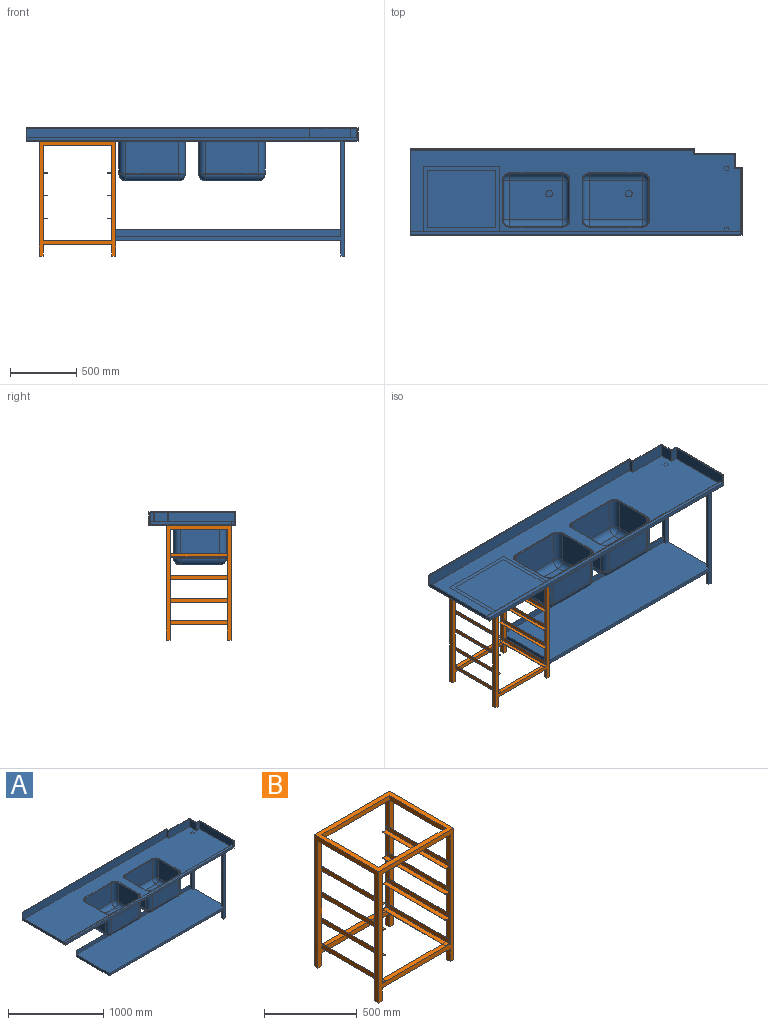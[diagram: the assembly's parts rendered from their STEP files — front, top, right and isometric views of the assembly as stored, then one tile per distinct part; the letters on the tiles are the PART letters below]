
ASSEMBLY  parts=2 mates=1
PART A: 143 faces, bbox 2500x650x965 mm
  f0: plane 715x30mm, normal (0,-1,0), area 21450mm2, adj f15,f94,f96,f121
  f1: plane 120x30mm, normal (-1,0,0), area 3600mm2, adj f93,f95,f97,f122
  f2: plane 715x30mm, normal (-1,0,0), area 21450mm2, adj f3,f15,f98,f121
  f3: plane 715x30mm, normal (0,1,0), area 21450mm2, adj f2,f15,f94,f121
  f4: plane 2488x28mm, normal (0,1,0), area 69664mm2, adj f5,f18,f32,f118
  f5: plane 2488x610mm, normal (0,0,1), area 1090860.9mm2, adj f4,f16,f17,f18,f19,f20,f21,f102
  f6: plane 650x100mm, normal (-1,0,0), area 20200mm2, adj f7,f8,f14,f15,f17,f32
  f7: plane 2500x100mm, normal (0,-1,0), area 75700mm2, adj f6,f8,f9,f15,f18,f32
  f8: plane 2500x650mm, normal (0,0,1), area 31400mm2, adj f6,f7,f9,f10,f11,f12,f13,f14
  f9: plane 510x100mm, normal (1,0,0), area 51000mm2, adj f7,f8,f10,f15
  f10: plane 100x50mm, normal (0,1,0), area 5000mm2, adj f8,f9,f11,f15
  f11: plane 105x100mm, normal (1,0,0), area 10500mm2, adj f8,f10,f12,f15
  f12: plane 305x100mm, normal (0,1,0), area 30500mm2, adj f8,f11,f13,f15
  f13: plane 100x35mm, normal (1,0,0), area 3500mm2, adj f8,f12,f14,f15
  f14: plane 2145x100mm, normal (0,1,0), area 214500mm2, adj f6,f8,f13,f15
  f15: plane 2500x650mm, normal (0,0,-1), area 1209817mm2, adj f0,f2,f3,f6,f7,f9,f10,f11
  f16: plane 98x35mm, normal (-1,0,0), area 3430mm2, adj f5,f8,f17,f21
  f17: plane 2135x98mm, normal (0,-1,0), area 209174mm2, adj f5,f6,f8,f16,f32,f118
  f18: plane 500x98mm, normal (-1,0,0), area 48160mm2, adj f4,f5,f7,f8,f19,f32
  f19: plane 98x50mm, normal (0,-1,0), area 4900mm2, adj f5,f8,f18,f20
  f20: plane 105x98mm, normal (-1,0,0), area 10290mm2, adj f5,f8,f19,f21
  f21: plane 305x98mm, normal (0,-1,0), area 29890mm2, adj f5,f8,f16,f20
  f22: plane 300x248mm, normal (-1,0,0), area 74400mm2, adj f15,f81,f87,f90
  f23: plane 400x248mm, normal (0,-1,0), area 99200mm2, adj f15,f79,f81,f82
  f24: plane 300x248mm, normal (1,0,0), area 74400mm2, adj f15,f79,f83,f84
  f25: plane 400x248mm, normal (0,1,0), area 99200mm2, adj f15,f84,f88,f90
  f26: plane 400x300mm, normal (0,0,-1), area 118036.5mm2, adj f82,f83,f87,f88,f92
  f27: plane 300x248mm, normal (-1,0,0), area 74400mm2, adj f15,f72,f76,f78
  f28: plane 400x248mm, normal (0,-1,0), area 99200mm2, adj f15,f69,f75,f78
  f29: plane 300x248mm, normal (1,0,0), area 74400mm2, adj f15,f67,f69,f70
  f30: plane 400x248mm, normal (0,1,0), area 99200mm2, adj f15,f67,f71,f72
  f31: plane 400x300mm, normal (0,0,-1), area 118036.5mm2, adj f70,f71,f75,f76,f91
  f32: plane 2490x640mm, normal (0,0,1), area 75920mm2, adj f4,f6,f7,f17,f18,f118
  f33: plane 396x296mm, normal (0,0,1), area 115252.5mm2, adj f46,f47,f51,f52,f92
  f34: plane 396x242mm, normal (0,-1,0), area 95832mm2, adj f45,f51,f54,f110
  f35: plane 296x242mm, normal (-1,0,0), area 71632mm2, adj f43,f45,f46,f114
  f36: plane 396x242mm, normal (0,1,0), area 95832mm2, adj f43,f47,f48,f117
  f37: plane 296x242mm, normal (1,0,0), area 71632mm2, adj f48,f52,f54,f113
  f38: plane 396x296mm, normal (0,0,1), area 115252.5mm2, adj f58,f59,f63,f64,f91
  f39: plane 396x242mm, normal (0,-1,0), area 95832mm2, adj f55,f57,f58,f102
  f40: plane 296x242mm, normal (-1,0,0), area 71632mm2, adj f55,f59,f60,f106
  f41: plane 396x242mm, normal (0,1,0), area 95832mm2, adj f60,f64,f66,f109
  f42: plane 296x242mm, normal (1,0,0), area 71632mm2, adj f57,f63,f66,f105
  f43: cylinder r=50mm len=242mm, axis (0,0,1), area 19006.6mm2, adj f35,f36,f44,f116
  f44: sphere r=50mm, area 3927mm2, adj f43,f46,f47
  f45: cylinder r=50mm len=242mm, axis (0,0,-1), area 19006.6mm2, adj f34,f35,f49,f112
  f46: cylinder r=50mm len=296mm, axis (0,1,0), area 23247.8mm2, adj f33,f35,f44,f49
  f47: cylinder r=50mm len=396mm, axis (1,0,0), area 31101.8mm2, adj f33,f36,f44,f50
  f48: cylinder r=50mm len=242mm, axis (0,0,-1), area 19006.6mm2, adj f36,f37,f50,f115
  f49: sphere r=50mm, area 3927mm2, adj f45,f46,f51
  f50: sphere r=50mm, area 3927mm2, adj f47,f48,f52
  f51: cylinder r=50mm len=396mm, axis (-1,0,0), area 31101.8mm2, adj f33,f34,f49,f53
  f52: cylinder r=50mm len=296mm, axis (0,-1,0), area 23247.8mm2, adj f33,f37,f50,f53
  f53: sphere r=50mm, area 3927mm2, adj f51,f52,f54
  f54: cylinder r=50mm len=242mm, axis (0,0,1), area 19006.6mm2, adj f34,f37,f53,f111
  f55: cylinder r=50mm len=242mm, axis (0,0,-1), area 19006.6mm2, adj f39,f40,f56,f104
  f56: sphere r=50mm, area 3927mm2, adj f55,f58,f59
  f57: cylinder r=50mm len=242mm, axis (0,0,1), area 19006.6mm2, adj f39,f42,f61,f103
  f58: cylinder r=50mm len=396mm, axis (-1,0,0), area 31101.8mm2, adj f38,f39,f56,f61
  f59: cylinder r=50mm len=296mm, axis (0,1,0), area 23247.8mm2, adj f38,f40,f56,f62
  f60: cylinder r=50mm len=242mm, axis (0,0,1), area 19006.6mm2, adj f40,f41,f62,f108
  f61: sphere r=50mm, area 3927mm2, adj f57,f58,f63
  f62: sphere r=50mm, area 3927mm2, adj f59,f60,f64
  f63: cylinder r=50mm len=296mm, axis (0,-1,0), area 23247.8mm2, adj f38,f42,f61,f65
  f64: cylinder r=50mm len=396mm, axis (1,0,0), area 31101.8mm2, adj f38,f41,f62,f65
  f65: sphere r=50mm, area 3927mm2, adj f63,f64,f66
  f66: cylinder r=50mm len=242mm, axis (0,0,-1), area 19006.6mm2, adj f41,f42,f65,f107
  f67: cylinder r=50mm len=248mm, axis (0,0,1), area 19477.9mm2, adj f15,f29,f30,f68
  f68: sphere r=50mm, area 3927mm2, adj f67,f70,f71
  f69: cylinder r=50mm len=248mm, axis (0,0,-1), area 19477.9mm2, adj f15,f28,f29,f73
  f70: cylinder r=50mm len=300mm, axis (0,-1,0), area 23561.9mm2, adj f29,f31,f68,f73
  f71: cylinder r=50mm len=400mm, axis (1,0,0), area 31415.9mm2, adj f30,f31,f68,f74
  f72: cylinder r=50mm len=248mm, axis (0,0,-1), area 19477.9mm2, adj f15,f27,f30,f74
  f73: sphere r=50mm, area 3927mm2, adj f69,f70,f75
  f74: sphere r=50mm, area 3927mm2, adj f71,f72,f76
  f75: cylinder r=50mm len=400mm, axis (-1,0,0), area 31415.9mm2, adj f28,f31,f73,f77
  f76: cylinder r=50mm len=300mm, axis (0,1,0), area 23561.9mm2, adj f27,f31,f74,f77
  f77: sphere r=50mm, area 3927mm2, adj f75,f76,f78
  f78: cylinder r=50mm len=248mm, axis (0,0,1), area 19477.9mm2, adj f15,f27,f28,f77
  f79: cylinder r=50mm len=248mm, axis (0,0,-1), area 19477.9mm2, adj f15,f23,f24,f80
  f80: sphere r=50mm, area 3927mm2, adj f79,f82,f83
  f81: cylinder r=50mm len=248mm, axis (0,0,1), area 19477.9mm2, adj f15,f22,f23,f85
  f82: cylinder r=50mm len=400mm, axis (-1,0,0), area 31415.9mm2, adj f23,f26,f80,f85
  f83: cylinder r=50mm len=300mm, axis (0,-1,0), area 23561.9mm2, adj f24,f26,f80,f86
  f84: cylinder r=50mm len=248mm, axis (0,0,1), area 19477.9mm2, adj f15,f24,f25,f86
  f85: sphere r=50mm, area 3927mm2, adj f81,f82,f87
  f86: sphere r=50mm, area 3927mm2, adj f83,f84,f88
  f87: cylinder r=50mm len=300mm, axis (0,1,0), area 23561.9mm2, adj f22,f26,f85,f89
  f88: cylinder r=50mm len=400mm, axis (1,0,0), area 31415.9mm2, adj f25,f26,f86,f89
  f89: sphere r=50mm, area 3927mm2, adj f87,f88,f90
  f90: cylinder r=50mm len=248mm, axis (0,0,-1), area 19477.9mm2, adj f15,f22,f25,f89
  f91: cylinder r=25mm len=50mm, axis (0,0,1), area 314.2mm2, adj f31,f38
  f92: cylinder r=25mm len=50mm, axis (0,0,1), area 314.2mm2, adj f26,f33
  f93: plane 1725x865mm, normal (0,1,0), area 161550mm2, adj f1,f15,f94,f96,f97,f119,f122,f123
  f94: plane 865x490mm, normal (1,0,0), area 64800mm2, adj f0,f3,f15,f93,f95,f97,f98,f100
  f95: plane 120x30mm, normal (0,-1,0), area 3600mm2, adj f1,f94,f97,f122
  f96: plane 715x30mm, normal (-1,0,0), area 21350mm2, adj f0,f15,f93,f119,f120,f121
  f97: plane 30x30mm, normal (0,0,-1), area 900mm2, adj f1,f93,f94,f95
  f98: plane 1725x865mm, normal (0,-1,0), area 76800mm2, adj f2,f15,f94,f99,f101,f121,f122,f123
  f99: plane 120x30mm, normal (-1,0,0), area 3600mm2, adj f98,f100,f101,f122
  f100: plane 120x30mm, normal (0,1,0), area 3600mm2, adj f94,f99,f101,f122
  f101: plane 30x30mm, normal (0,0,-1), area 900mm2, adj f94,f98,f99,f100
  f102: cylinder r=6mm len=396mm, axis (1,0,0), area 3732.2mm2, adj f5,f39,f103,f104
  f103: torus R=56mm, axis (0,0,1), area 772.5mm2, adj f5,f57,f102,f105
  f104: torus R=56mm, axis (0,0,1), area 772.5mm2, adj f5,f55,f102,f106
  f105: cylinder r=6mm len=296mm, axis (0,1,0), area 2789.7mm2, adj f5,f42,f103,f107
  f106: cylinder r=6mm len=296mm, axis (0,-1,0), area 2789.7mm2, adj f5,f40,f104,f108
  f107: torus R=56mm, axis (0,0,1), area 772.5mm2, adj f5,f66,f105,f109
  f108: torus R=56mm, axis (0,0,1), area 772.5mm2, adj f5,f60,f106,f109
  f109: cylinder r=6mm len=396mm, axis (-1,0,0), area 3732.2mm2, adj f5,f41,f107,f108
  f110: cylinder r=6mm len=396mm, axis (1,0,0), area 3732.2mm2, adj f5,f34,f111,f112
  f111: torus R=56mm, axis (0,0,1), area 772.5mm2, adj f5,f54,f110,f113
  f112: torus R=56mm, axis (0,0,1), area 772.5mm2, adj f5,f45,f110,f114
  f113: cylinder r=6mm len=296mm, axis (0,1,0), area 2789.7mm2, adj f5,f37,f111,f115
  f114: cylinder r=6mm len=296mm, axis (0,-1,0), area 2789.7mm2, adj f5,f35,f112,f116
  f115: torus R=56mm, axis (0,0,1), area 772.5mm2, adj f5,f48,f113,f117
  f116: torus R=56mm, axis (0,0,1), area 772.5mm2, adj f5,f43,f114,f117
  f117: cylinder r=6mm len=396mm, axis (-1,0,0), area 3732.2mm2, adj f5,f36,f115,f116
  f118: plane 610x28mm, normal (1,0,0), area 17080mm2, adj f4,f5,f17,f32
  f119: plane 1695x2mm, normal (0,0,1), area 3390mm2, adj f93,f96,f120,f123
  f120: plane 1695x50mm, normal (0,-1,0), area 84750mm2, adj f96,f119,f121,f123
  f121: plane 1725x488mm, normal (0,0,1), area 840060mm2, adj f0,f2,f3,f94,f96,f98,f120,f123
  f122: plane 1725x490mm, normal (0,0,-1), area 843450mm2, adj f1,f93,f94,f95,f98,f99,f100,f123
  f123: plane 490x80mm, normal (-1,0,0), area 14800mm2, adj f93,f98,f119,f120,f121,f122
  f124: plane 2496x646mm, normal (0,0,1), area 83556mm2, adj f125,f126,f127,f129,f130,f131,f132,f133
  f125: plane 96x6mm, normal (1,0,0), area 576mm2, adj f124,f128,f134,f136
  f126: plane 26x26mm, normal (1,0,0), area 676mm2, adj f124,f127,f137,f142
  f127: plane 2496x96mm, normal (0,1,0), area 65316mm2, adj f124,f126,f128,f129,f138,f142
  f128: plane 2496x646mm, normal (0,0,-1), area 18816mm2, adj f125,f127,f129,f130,f131,f132,f133,f134
  f129: plane 506x96mm, normal (-1,0,0), area 48576mm2, adj f124,f127,f128,f130
  f130: plane 96x50mm, normal (0,-1,0), area 4800mm2, adj f124,f128,f129,f131
  f131: plane 105x96mm, normal (-1,0,0), area 10080mm2, adj f124,f128,f130,f132
  f132: plane 305x96mm, normal (0,-1,0), area 29280mm2, adj f124,f128,f131,f133
  f133: plane 96x35mm, normal (-1,0,0), area 3360mm2, adj f124,f128,f132,f134
  f134: plane 2141x96mm, normal (0,-1,0), area 205536mm2, adj f124,f125,f128,f133
  f135: plane 96x35mm, normal (1,0,0), area 3360mm2, adj f124,f128,f136,f141
  f136: plane 2135x96mm, normal (0,1,0), area 204960mm2, adj f124,f125,f128,f135
  f137: plane 2490x26mm, normal (0,-1,0), area 64740mm2, adj f124,f126,f138,f142
  f138: plane 500x96mm, normal (1,0,0), area 47324mm2, adj f124,f127,f128,f137,f139,f142
  f139: plane 96x50mm, normal (0,1,0), area 4800mm2, adj f124,f128,f138,f140
  f140: plane 105x96mm, normal (1,0,0), area 10080mm2, adj f124,f128,f139,f141
  f141: plane 305x96mm, normal (0,1,0), area 29280mm2, adj f124,f128,f135,f140
  f142: plane 2490x26mm, normal (0,0,-1), area 64740mm2, adj f126,f127,f137,f138
PART B: 127 faces, bbox 575x490x865 mm
  f0: plane 720x30mm, normal (-1,0,0), area 18621.5mm2, adj f3,f18,f20,f26,f82,f84,f90,f93
  f1: plane 515x30mm, normal (0,0,1), area 13960.7mm2, adj f5,f6,f8,f12,f35,f38,f39,f83
  f2: plane 720x30mm, normal (1,0,0), area 18621.5mm2, adj f3,f18,f20,f26,f34,f36,f42,f45
  f3: plane 515x30mm, normal (0,0,1), area 13960.7mm2, adj f0,f2,f18,f20,f36,f38,f40,f84
  f4: plane 515x30mm, normal (0,1,0), area 15450mm2, adj f10,f17,f28,f29
  f5: plane 835x575mm, normal (0,1,0), area 65550mm2, adj f1,f6,f7,f9,f11,f12,f13,f14
  f6: plane 720x30mm, normal (1,0,0), area 18621.5mm2, adj f1,f5,f8,f17,f34,f35,f41,f45
  f7: plane 865x490mm, normal (-1,0,0), area 64800mm2, adj f5,f8,f10,f11,f18,f20,f22,f27
  f8: plane 865x575mm, normal (0,-1,0), area 82800mm2, adj f1,f6,f7,f9,f10,f11,f12,f13
  f9: plane 85x30mm, normal (1,0,0), area 2550mm2, adj f5,f8,f11,f16
  f10: plane 575x490mm, normal (0,0,1), area 60300mm2, adj f4,f7,f8,f13,f20,f21,f28,f29
  f11: plane 30x30mm, normal (0,0,-1), area 900mm2, adj f5,f7,f8,f9
  f12: plane 720x30mm, normal (-1,0,0), area 18621.5mm2, adj f1,f5,f8,f17,f82,f83,f89,f93
  f13: plane 865x490mm, normal (1,0,0), area 64800mm2, adj f5,f8,f10,f15,f18,f20,f24,f30
  f14: plane 85x30mm, normal (-1,0,0), area 2550mm2, adj f5,f8,f15,f16
  f15: plane 30x30mm, normal (0,0,-1), area 900mm2, adj f5,f8,f13,f14
  f16: plane 515x30mm, normal (0,0,-1), area 15450mm2, adj f5,f8,f9,f14
  f17: plane 515x30mm, normal (0,0,-1), area 15450mm2, adj f4,f6,f8,f12
  f18: plane 835x575mm, normal (0,-1,0), area 65550mm2, adj f0,f2,f3,f7,f13,f19,f22,f23
  f19: plane 85x30mm, normal (1,0,0), area 2550mm2, adj f18,f20,f22,f25
  f20: plane 865x575mm, normal (0,1,0), area 82800mm2, adj f0,f2,f3,f7,f10,f13,f19,f22
  f21: plane 515x30mm, normal (0,-1,0), area 15450mm2, adj f10,f26,f28,f29
  f22: plane 30x30mm, normal (0,0,-1), area 900mm2, adj f7,f18,f19,f20
  f23: plane 85x30mm, normal (-1,0,0), area 2550mm2, adj f18,f20,f24,f25
  f24: plane 30x30mm, normal (0,0,-1), area 900mm2, adj f13,f18,f20,f23
  f25: plane 515x30mm, normal (0,0,-1), area 15450mm2, adj f18,f19,f20,f23
  f26: plane 515x30mm, normal (0,0,-1), area 15450mm2, adj f0,f2,f20,f21
  f27: plane 430x30mm, normal (0,0,-1), area 12900mm2, adj f5,f7,f18,f28
  f28: plane 430x30mm, normal (1,0,0), area 12900mm2, adj f4,f10,f21,f27
  f29: plane 430x30mm, normal (-1,0,0), area 12900mm2, adj f4,f10,f21,f30
  f30: plane 430x30mm, normal (0,0,-1), area 12900mm2, adj f5,f13,f18,f29
  f31: plane 430x30mm, normal (0,0,-1), area 12900mm2, adj f5,f18,f32,f38
  f32: plane 430x30mm, normal (-1,0,0), area 12900mm2, adj f5,f18,f31,f34
  f33: plane 480x28.5mm, normal (1,0,0), area 13669.3mm2, adj f34,f35,f36,f37,f41,f42
  f34: plane 470x1.5mm, normal (0,0,1), area 705mm2, adj f2,f6,f32,f33,f41,f42
  f35: plane 25x25mm, normal (0,-1,0), area 72.8mm2, adj f1,f6,f33,f37,f39,f41
  f36: plane 25x25mm, normal (0,1,0), area 72.8mm2, adj f2,f3,f33,f37,f40,f42
  f37: plane 480x28.5mm, normal (0,0,1), area 13669.3mm2, adj f33,f35,f36,f38,f39,f40
  f38: plane 470x1.5mm, normal (1,0,0), area 705mm2, adj f1,f3,f31,f37,f39,f40
  f39: cylinder r=5mm len=5mm, axis (0,0,1), area 11.8mm2, adj f1,f35,f37,f38
  f40: cylinder r=5mm len=5mm, axis (0,0,-1), area 11.8mm2, adj f3,f36,f37,f38
  f41: cylinder r=5mm len=5mm, axis (-1,0,0), area 11.8mm2, adj f6,f33,f34,f35
  f42: cylinder r=5mm len=5mm, axis (1,0,0), area 11.8mm2, adj f2,f33,f34,f36
  f43: plane 430x30mm, normal (-1,0,0), area 12900mm2, adj f5,f18,f45,f47
  f44: plane 480x28.5mm, normal (1,0,0), area 13669.3mm2, adj f45,f46,f48,f49,f53,f54
  f45: plane 470x1.5mm, normal (0,0,1), area 705mm2, adj f2,f6,f43,f44,f53,f54
  f46: plane 25x25mm, normal (0,-1,0), area 72.8mm2, adj f6,f44,f47,f49,f52,f54
  f47: plane 480x30mm, normal (0,0,-1), area 14389.3mm2, adj f2,f6,f43,f46,f48,f50,f51,f52
  f48: plane 25x25mm, normal (0,1,0), area 72.8mm2, adj f2,f44,f47,f49,f51,f53
  f49: plane 480x28.5mm, normal (0,0,1), area 13669.3mm2, adj f44,f46,f48,f50,f51,f52
  f50: plane 470x1.5mm, normal (1,0,0), area 705mm2, adj f47,f49,f51,f52
  f51: cylinder r=5mm len=5mm, axis (0,0,-1), area 11.8mm2, adj f47,f48,f49,f50
  f52: cylinder r=5mm len=5mm, axis (0,0,1), area 11.8mm2, adj f46,f47,f49,f50
  f53: cylinder r=5mm len=5mm, axis (1,0,0), area 11.8mm2, adj f2,f44,f45,f48
  f54: cylinder r=5mm len=5mm, axis (-1,0,0), area 11.8mm2, adj f6,f44,f45,f46
  f55: plane 430x30mm, normal (-1,0,0), area 12900mm2, adj f5,f18,f57,f59
  f56: plane 480x28.5mm, normal (1,0,0), area 13669.3mm2, adj f57,f58,f60,f61,f65,f66
  f57: plane 470x1.5mm, normal (0,0,1), area 705mm2, adj f2,f6,f55,f56,f65,f66
  f58: plane 25x25mm, normal (0,-1,0), area 72.8mm2, adj f6,f56,f59,f61,f64,f65
  f59: plane 480x30mm, normal (0,0,-1), area 14389.3mm2, adj f2,f6,f55,f58,f60,f62,f63,f64
  f60: plane 25x25mm, normal (0,1,0), area 72.8mm2, adj f2,f56,f59,f61,f63,f66
  f61: plane 480x28.5mm, normal (0,0,1), area 13669.3mm2, adj f56,f58,f60,f62,f63,f64
  f62: plane 470x1.5mm, normal (1,0,0), area 705mm2, adj f59,f61,f63,f64
  f63: cylinder r=5mm len=5mm, axis (0,0,-1), area 11.8mm2, adj f59,f60,f61,f62
  f64: cylinder r=5mm len=5mm, axis (0,0,1), area 11.8mm2, adj f58,f59,f61,f62
  f65: cylinder r=5mm len=5mm, axis (-1,0,0), area 11.8mm2, adj f6,f56,f57,f58
  f66: cylinder r=5mm len=5mm, axis (1,0,0), area 11.8mm2, adj f2,f56,f57,f60
  f67: plane 430x30mm, normal (-1,0,0), area 12900mm2, adj f5,f18,f69,f71
  f68: plane 480x28.5mm, normal (1,0,0), area 13669.3mm2, adj f69,f70,f72,f73,f77,f78
  f69: plane 470x1.5mm, normal (0,0,1), area 705mm2, adj f2,f6,f67,f68,f77,f78
  f70: plane 25x25mm, normal (0,-1,0), area 72.7mm2, adj f6,f68,f71,f73,f76,f77
  f71: plane 480x30mm, normal (0,0,-1), area 14389.3mm2, adj f2,f6,f67,f70,f72,f74,f75,f76
  f72: plane 25x25mm, normal (0,1,0), area 72.7mm2, adj f2,f68,f71,f73,f75,f78
  f73: plane 480x28.5mm, normal (0,0,1), area 13669.3mm2, adj f68,f70,f72,f74,f75,f76
  f74: plane 470x1.5mm, normal (1,0,0), area 705mm2, adj f71,f73,f75,f76
  f75: cylinder r=5mm len=5mm, axis (0,0,-1), area 11.8mm2, adj f71,f72,f73,f74
  f76: cylinder r=5mm len=5mm, axis (0,0,1), area 11.8mm2, adj f70,f71,f73,f74
  f77: cylinder r=5mm len=5mm, axis (-1,0,0), area 11.8mm2, adj f6,f68,f69,f70
  f78: cylinder r=5mm len=5mm, axis (1,0,0), area 11.8mm2, adj f2,f68,f69,f72
  f79: plane 430x30mm, normal (0,0,-1), area 12900mm2, adj f5,f18,f80,f86
  f80: plane 430x30mm, normal (1,0,0), area 12900mm2, adj f5,f18,f79,f82
  f81: plane 480x28.5mm, normal (-1,0,0), area 13669.3mm2, adj f82,f83,f84,f85,f89,f90
  f82: plane 470x1.5mm, normal (0,0,1), area 705mm2, adj f0,f12,f80,f81,f89,f90
  f83: plane 25x25mm, normal (0,-1,0), area 72.8mm2, adj f1,f12,f81,f85,f87,f89
  f84: plane 25x25mm, normal (0,1,0), area 72.8mm2, adj f0,f3,f81,f85,f88,f90
  f85: plane 480x28.5mm, normal (0,0,1), area 13669.3mm2, adj f81,f83,f84,f86,f87,f88
  f86: plane 470x1.5mm, normal (-1,0,0), area 705mm2, adj f1,f3,f79,f85,f87,f88
  f87: cylinder r=5mm len=5mm, axis (0,0,1), area 11.8mm2, adj f1,f83,f85,f86
  f88: cylinder r=5mm len=5mm, axis (0,0,-1), area 11.8mm2, adj f3,f84,f85,f86
  f89: cylinder r=5mm len=5mm, axis (1,0,0), area 11.8mm2, adj f12,f81,f82,f83
  f90: cylinder r=5mm len=5mm, axis (-1,0,0), area 11.8mm2, adj f0,f81,f82,f84
  f91: plane 430x30mm, normal (1,0,0), area 12900mm2, adj f5,f18,f93,f95
  f92: plane 480x28.5mm, normal (-1,0,0), area 13669.3mm2, adj f93,f94,f96,f97,f101,f102
  f93: plane 470x1.5mm, normal (0,0,1), area 705mm2, adj f0,f12,f91,f92,f101,f102
  f94: plane 25x25mm, normal (0,-1,0), area 72.8mm2, adj f12,f92,f95,f97,f100,f102
  f95: plane 480x30mm, normal (0,0,-1), area 14389.3mm2, adj f0,f12,f91,f94,f96,f98,f99,f100
  f96: plane 25x25mm, normal (0,1,0), area 72.8mm2, adj f0,f92,f95,f97,f99,f101
  f97: plane 480x28.5mm, normal (0,0,1), area 13669.3mm2, adj f92,f94,f96,f98,f99,f100
  f98: plane 470x1.5mm, normal (-1,0,0), area 705mm2, adj f95,f97,f99,f100
  f99: cylinder r=5mm len=5mm, axis (0,0,-1), area 11.8mm2, adj f95,f96,f97,f98
  f100: cylinder r=5mm len=5mm, axis (0,0,1), area 11.8mm2, adj f94,f95,f97,f98
  f101: cylinder r=5mm len=5mm, axis (-1,0,0), area 11.8mm2, adj f0,f92,f93,f96
  f102: cylinder r=5mm len=5mm, axis (1,0,0), area 11.8mm2, adj f12,f92,f93,f94
  f103: plane 430x30mm, normal (1,0,0), area 12900mm2, adj f5,f18,f105,f107
  f104: plane 480x28.5mm, normal (-1,0,0), area 13669.3mm2, adj f105,f106,f108,f109,f113,f114
  f105: plane 470x1.5mm, normal (0,0,1), area 705mm2, adj f0,f12,f103,f104,f113,f114
  f106: plane 25x25mm, normal (0,-1,0), area 72.8mm2, adj f12,f104,f107,f109,f112,f113
  f107: plane 480x30mm, normal (0,0,-1), area 14389.3mm2, adj f0,f12,f103,f106,f108,f110,f111,f112
  f108: plane 25x25mm, normal (0,1,0), area 72.8mm2, adj f0,f104,f107,f109,f111,f114
  f109: plane 480x28.5mm, normal (0,0,1), area 13669.3mm2, adj f104,f106,f108,f110,f111,f112
  f110: plane 470x1.5mm, normal (-1,0,0), area 705mm2, adj f107,f109,f111,f112
  f111: cylinder r=5mm len=5mm, axis (0,0,-1), area 11.8mm2, adj f107,f108,f109,f110
  f112: cylinder r=5mm len=5mm, axis (0,0,1), area 11.8mm2, adj f106,f107,f109,f110
  f113: cylinder r=5mm len=5mm, axis (1,0,0), area 11.8mm2, adj f12,f104,f105,f106
  f114: cylinder r=5mm len=5mm, axis (-1,0,0), area 11.8mm2, adj f0,f104,f105,f108
  f115: plane 430x30mm, normal (1,0,0), area 12900mm2, adj f5,f18,f117,f119
  f116: plane 480x28.5mm, normal (-1,0,0), area 13669.3mm2, adj f117,f118,f120,f121,f125,f126
  f117: plane 470x1.5mm, normal (0,0,1), area 705mm2, adj f0,f12,f115,f116,f125,f126
  f118: plane 25x25mm, normal (0,-1,0), area 72.7mm2, adj f12,f116,f119,f121,f124,f125
  f119: plane 480x30mm, normal (0,0,-1), area 14389.3mm2, adj f0,f12,f115,f118,f120,f122,f123,f124
  f120: plane 25x25mm, normal (0,1,0), area 72.7mm2, adj f0,f116,f119,f121,f123,f126
  f121: plane 480x28.5mm, normal (0,0,1), area 13669.3mm2, adj f116,f118,f120,f122,f123,f124
  f122: plane 470x1.5mm, normal (-1,0,0), area 705mm2, adj f119,f121,f123,f124
  f123: cylinder r=5mm len=5mm, axis (0,0,-1), area 11.8mm2, adj f119,f120,f121,f122
  f124: cylinder r=5mm len=5mm, axis (0,0,1), area 11.8mm2, adj f118,f119,f121,f122
  f125: cylinder r=5mm len=5mm, axis (1,0,0), area 11.8mm2, adj f12,f116,f117,f118
  f126: cylinder r=5mm len=5mm, axis (-1,0,0), area 11.8mm2, adj f0,f116,f117,f120
PLACE A t=(-519.57,-163.49,-7.8)mm
PLACE B t=(-132.07,111.51,-872.8)mm
MATE fastened B.f10 <-> A.f15  axis (0,0,1) through (-419.57,-133.49,-7.8)mm
